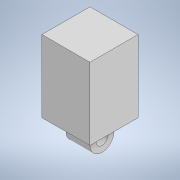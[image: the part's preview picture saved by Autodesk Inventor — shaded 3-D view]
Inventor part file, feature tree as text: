
AUTODESK INVENTOR PART (.ipt)
format: ipt  version: 2022 (Build 260153000, 153)  size: 130,560 bytes
history: native  units: mm
features: extrude x3, sketch x3, fillet x1
ambient origin geometry x8: Origin, YZ Plane, XZ Plane, XY Plane, X Axis, Y Axis, Z Axis, Center Point
bodies: Solide1 (feature_tree)
feature tree (7):
  extrude  "Extrusion1"  Depth=20.0mm
  extrude  "Extrusion2"  Depth=30.0mm
  extrude  "Extrusion3"  Depth=20.0mm TaperAngle=0.0deg
  fillet  "Congé1"  Radius=10.0mm
  sketch  "Esquisse1"
  sketch  "Esquisse3"
  sketch  "Esquisse4"
